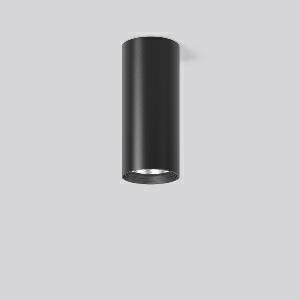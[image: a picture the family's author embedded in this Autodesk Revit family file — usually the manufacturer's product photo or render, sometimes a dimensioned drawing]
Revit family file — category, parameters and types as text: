
# Revit family: heledon_mini_a_931200_003_1_76_b2be
name_source: partatom
category: Lighting Fixtures
units: mm (PartAtom-declared; Revit-internal decimal feet)

## family parameters
Cut with Voids When Loaded = No
Host = Face
Light Source = No
Part Type = Normal
Room Calculation Point = No
Round Connector Dimension = Use Diameter
Shared = No

## types (1)
- HELEDON mini A (1 x LED Modul 940, 2700 lm, 4000)
    Apparent Load = 20 VA
    Approval mark = CE
    CIE Flux Codes = 100 100 100 100 100
    Color Rendering = 92
    Color Temperature = 4000
    Default Elevation = 1800 mm
    Description = Series: HELEDON mini
Cylindrical surface-mounted downlight. Housing: die-cast aluminium, powder-coated. Internal ceiling frame polycarbonate with bayonet mounting. Black plastic ring and recessed LED to prevent glare from the side. Optical assembly with reflector made of MIRO-Silver with 98% total light reflection for outstanding efficiency - can be changed without tools. Best colour rendering index Ra>90. Suitable for Ceiling mounting. Easy installation with a separate ceiling frame with bayonet mounting and plug connection. Driver integrated. Connected via plug-in connector. High quality converter without flickering and stroboscopic effect. The following accessories can be mounted without use of tools: interchangeable lenses, decorative glasses, honeycomb louvre, clear and frosted diffusers, white interchangeable plastic ring. 
Colour: deep black, matt (RAL 9005)
Diameter: 87 mm
Height: 197 mm
Lamp: LED
Socket: without socket
Colour temperature: 4000K
Colour rendering index (CRI): 92
System power: 20 W
Rated luminous flux: 2700 lm
Luminous efficiency: 135 lm/W
Control gear: Converter, dimmable, DALI
Protection class: I
Type of protection: IP 20
    Height = 197 mm
    Lamp = 1 x LED Modul 940
    Lamp Light Flux = 2700 lm
    Lamp count = 1
    Length = 87 mm
    Lifetime = 50000 h
    Luminous efficacy = 135 lm/W
    Manufacturer = RZB
    ModVariant = No
    Model = 931200.003.1.76
    Mounting Place = Ceiling
    Mounting Type = Surface mounted
    Number of Poles = 1
    OnlyDefault = Yes
    Power Factor = 1
    Product Name = HELEDON mini A
    Product group = Surface mounted downlights
    ProductGroupID = 302
    Protection Class = Protection class I
    Protection Degree = IP 20
    RLX_Detail_Level = 1
    RLX_Emergency_Light_Flux = 0 lm
    RLX_Emergency_Type = 0
    RLX_Emergency_Type_DB = No
    RlxData = <blob elided: 106185 chars, md5=88382155>
    Socket = socket
    Standby Power = 0 W
    System Light Flux = 2700 lm
    System Power = 20 W
    Type Comments = Product without accessories
    Type Image = 931188.003.jpg
    URL = http://relux.com
    VarID = ---
    Voltage = 230 V
    Voltage Range = 220-240 V
    Weight = 0.00 kg
    Width = 0 mm  [stored 0 ft]

note: [stored X ft] marks values corroborated as IEEE doubles in the binary element streams (Revit-internal decimal feet)

## geometry (parser evidence)
native form markers: Blend x4, Sweep x11
no freeform markers — native parametric forms only
